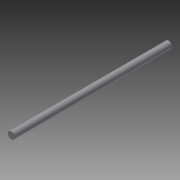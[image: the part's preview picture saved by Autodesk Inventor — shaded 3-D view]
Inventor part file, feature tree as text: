
AUTODESK INVENTOR PART (.ipt)
format: ipt  version: 2014 (Build 180170000, 170)  size: 65,536 bytes
history: native  units: in
note: dims shown in document units (in); Inventor stores cm internally (conversion verified against a paired STEP export)
features: extrude x1, sketch x1
ambient origin geometry x8: Origin, YZ Plane, XZ Plane, XY Plane, X Axis, Y Axis, Z Axis, Center Point
bodies: Solid1 (feature_tree)
feature tree (2):
  extrude  "Extrusion1"  Depth=11.25in TaperAngle=0.0deg
  sketch  "Sketch1"  dims[d0=0.5in d1=11.25in d2=0.0in]
